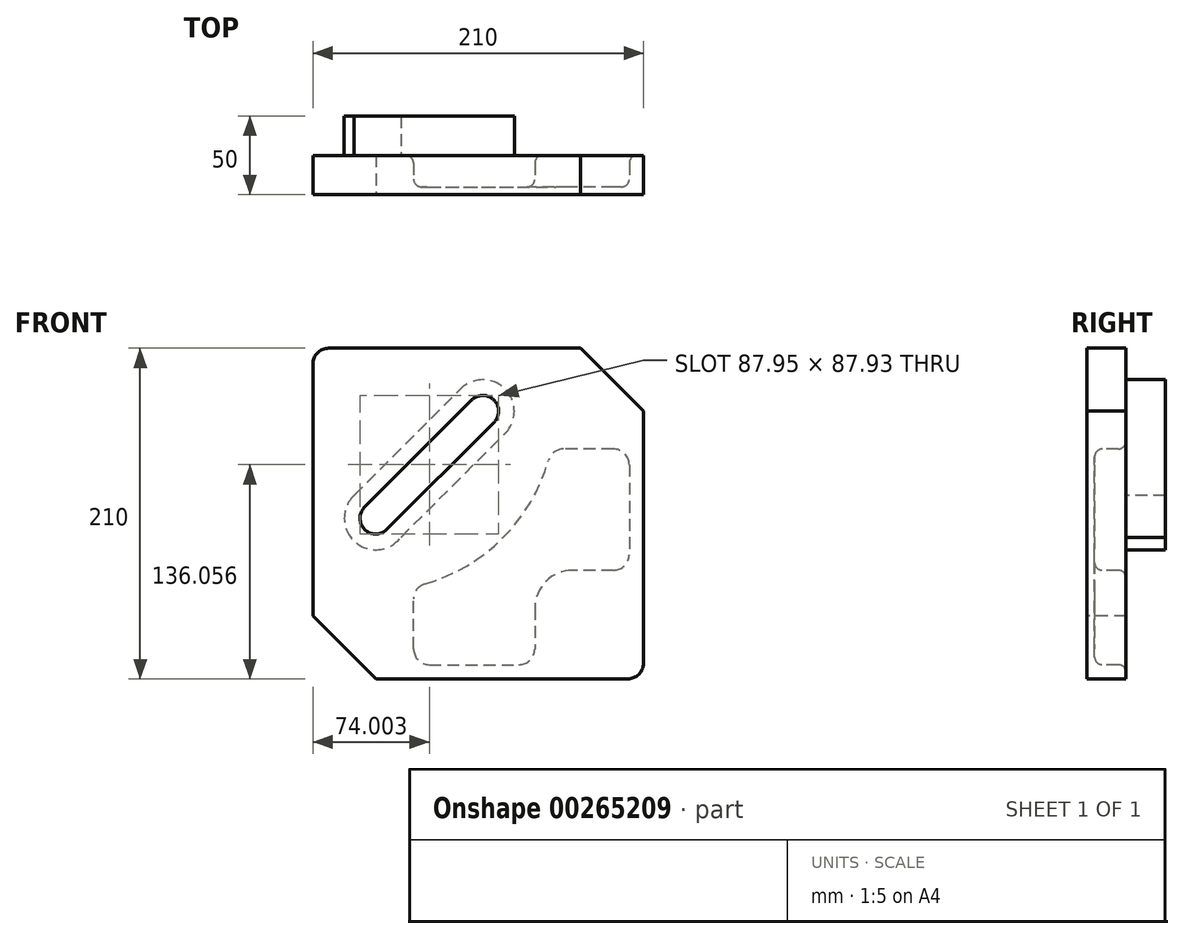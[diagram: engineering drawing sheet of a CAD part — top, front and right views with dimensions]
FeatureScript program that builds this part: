
annotation { "Feature Type Name" : "Feature", "Feature Type Description" : "" }
export const myFeature = defineFeature(function(context is Context, id is Id, definition is map)
    precondition{}
    {
        {
            var Q0;
            Q0=qCreatedBy(makeId("Front.planeOp"),FACE);
            var sketch = newSketch(context, id + "F0", { "sketchPlane" : qUnion([Q0])});
            skLineSegment(sketch, "E0", {"start": v(62.02, 39.98) * mm, "end": v(102.02, -0.02) * mm});
            skPoint(sketch, "E1.end.orphan", {"position": v(-107.98, -130.02) * mm});
            skLineSegment(sketch, "E2", {"start": v(62.02, 39.98) * mm, "end": v(-97.98, 39.98) * mm});
            skLineSegment(sketch, "E3", {"start": v(102.02, -0.02) * mm, "end": v(102.02, -160.02) * mm});
            skLineSegment(sketch, "E4", {"start": v(92.02, -170.02) * mm, "end": v(-67.98, -170.02) * mm});
            skLineSegment(sketch, "E5", {"start": v(-107.98, 29.98) * mm, "end": v(-107.98, -130.02) * mm});
            skLineSegment(sketch, "E6", {"start": v(-67.98, -170.02) * mm, "end": v(-107.98, -130.02) * mm});
            skArc(sketch, "E7", {"start": v(7.06, -7.08) * mm, "mid": v(7.07, 7.07) * mm, "end": v(-7.07, 7.07) * mm});
            skArc(sketch, "E8", {"start": v(-74.7, -60.61) * mm, "mid": v(-75.75, -74.31) * mm, "end": v(-62.14, -76.13) * mm});
            skArc(sketch, "E9", {"start": v(-81.65, -53.41) * mm, "mid": v(-81.42, -82.83) * mm, "end": v(-52.11, -80.19) * mm});
            skArc(sketch, "E10", {"start": v(14.12, -14.16) * mm, "mid": v(14.15, 14.13) * mm, "end": v(-14.15, 14.14) * mm});
            skLineSegment(sketch, "E11", {"start": v(-52.11, -80.19) * mm, "end": v(14.12, -14.16) * mm});
            skLineSegment(sketch, "E12", {"start": v(-81.65, -53.41) * mm, "end": v(-14.15, 14.14) * mm});
            skLineSegment(sketch, "E13", {"start": v(-74.7, -60.61) * mm, "end": v(-7.07, 7.07) * mm});
            skLineSegment(sketch, "E14", {"start": v(-62.14, -76.13) * mm, "end": v(7.06, -7.08) * mm});
            skPoint(sketch, "E15.orphan", {"position": v(14.16, 0) * mm});
            skPoint(sketch, "E16.orphan", {"position": v(0, 14.15) * mm});
            skPoint(sketch, "E17.visualSharp", {"position": v(-107.98, 39.98) * mm});
            skArc(sketch, "E17.filletArc", {"start": v(-97.98, 39.98) * mm, "mid": v(-105.06, 37.06) * mm, "end": v(-107.98, 29.98) * mm});
            skPoint(sketch, "E18.visualSharp", {"position": v(102.02, -170.02) * mm});
            skArc(sketch, "E18.filletArc", {"start": v(92.02, -170.02) * mm, "mid": v(99.09, -167.09) * mm, "end": v(102.02, -160.02) * mm});
            skLineSegment(sketch, "E19", {"start": v(83.02, -101.02) * mm, "end": v(57.02, -101.02) * mm});
            skLineSegment(sketch, "E20", {"start": v(33.02, -125.02) * mm, "end": v(33.02, -151.02) * mm});
            skPoint(sketch, "E21.visualSharp", {"position": v(33.02, -101.02) * mm});
            skArc(sketch, "E21.filletArc", {"start": v(57.02, -101.02) * mm, "mid": v(40.05, -108.05) * mm, "end": v(33.02, -125.02) * mm});
            skLineSegment(sketch, "E22", {"start": v(-43.98, -151.02) * mm, "end": v(-43.98, -119.26) * mm});
            skLineSegment(sketch, "E23", {"start": v(83.02, -24.02) * mm, "end": v(51.26, -24.02) * mm});
            skLineSegment(sketch, "E24", {"start": v(93.02, -34.02) * mm, "end": v(93.02, -91.02) * mm});
            skLineSegment(sketch, "E25", {"start": v(-33.98, -161.02) * mm, "end": v(23.02, -161.02) * mm});
            skPoint(sketch, "E26.newPointA", {"position": v(33.02, -170.02) * mm});
            skArc(sketch, "E26.filletArc", {"start": v(23.02, -161.02) * mm, "mid": v(30.09, -158.09) * mm, "end": v(33.02, -151.02) * mm});
            skPoint(sketch, "E27.newPointB", {"position": v(102.02, -101.02) * mm});
            skArc(sketch, "E27.filletArc", {"start": v(83.02, -101.02) * mm, "mid": v(90.09, -98.09) * mm, "end": v(93.02, -91.02) * mm});
            skPoint(sketch, "E28.newPointA", {"position": v(102.02, -24.02) * mm});
            skArc(sketch, "E28.filletArc", {"start": v(93.02, -34.02) * mm, "mid": v(90.09, -26.94) * mm, "end": v(83.02, -24.02) * mm});
            skPoint(sketch, "E29.newPointA", {"position": v(-43.98, -170.02) * mm});
            skArc(sketch, "E29.filletArc", {"start": v(-43.98, -151.02) * mm, "mid": v(-41.06, -158.09) * mm, "end": v(-33.98, -161.02) * mm});
            skPoint(sketch, "E30.orphan", {"position": v(33.02, -24.02) * mm});
            skArc(sketch, "E31.trimOffspring", {"start": v(-36.73, -109.65) * mm, "mid": v(12.63, -80.63) * mm, "end": v(41.65, -31.27) * mm});
            skPoint(sketch, "E32.visualSharp", {"position": v(43.46, -24.02) * mm});
            skArc(sketch, "E32.filletArc", {"start": v(51.26, -24.02) * mm, "mid": v(45.24, -26.03) * mm, "end": v(41.65, -31.27) * mm});
            skPoint(sketch, "E33.newPointB", {"position": v(-43.98, -101.02) * mm});
            skArc(sketch, "E33.filletArc", {"start": v(-36.73, -109.65) * mm, "mid": v(-41.97, -113.24) * mm, "end": v(-43.98, -119.26) * mm});
            skPoint(sketch, "E34.end.orphan", {"position": v(102.02, -33.02) * mm});
            skSolve(sketch);
        }
        {
            var Q0;
            Q0=makeQuery(id+"F0.imprint","IMPRINT",FACE,{"disambiguationData":[TD([[makeQuery(id+"F0.imprint","IMPRINT",EDGE,{"derivedFrom":sQuery(id+"F0.wireOp",EDGE,"E7")}),-1.0]])]});
            extrude(context, id + "F1", {"entities" : qUnion([Q0]), "oppositeDirection" : true, "depth" : 50 * mm});
        }
        {
            var Q0;
            Q0 = qSketchRegion(id + "F0", true);
            extrude(context, id + "F2", {"entities" : qUnion([Q0]), "operationType" : NewBodyOperationType.ADD, "oppositeDirection" : true, "depth" : 25 * mm});
        }
        {
            var Q0;
            {var subQ0=sQuery(id+"F0.wireOp",EDGE,"E12");var subQ1=sQuery(id+"F0.wireOp",EDGE,"E11");var subQ2=sQuery(id+"F0.wireOp",EDGE,"E10");var subQ3=sQuery(id+"F0.wireOp",EDGE,"E9");Q0=makeQuery(id+"F2.boolean.opBoolean","MERGE",FACE,{"derivedFrom":[makeQuery(id+"F1.opExtrude","CAP_FACE",FACE,{"disambiguationData":[OSD([sQuery(id+"F0.wireOp",EDGE,"E7"),sQuery(id+"F0.wireOp",EDGE,"E8"),subQ3,subQ2,subQ1,subQ0,sQuery(id+"F0.wireOp",EDGE,"E13"),sQuery(id+"F0.wireOp",EDGE,"E14")])],"isStart":true}),makeQuery(id+"F2.opExtrude","CAP_FACE",FACE,{"disambiguationData":[OSD([sQuery(id+"F0.wireOp",EDGE,"E0"),sQuery(id+"F0.wireOp",EDGE,"E2"),sQuery(id+"F0.wireOp",EDGE,"E3"),sQuery(id+"F0.wireOp",EDGE,"E4"),sQuery(id+"F0.wireOp",EDGE,"E5"),sQuery(id+"F0.wireOp",EDGE,"E6"),subQ3,subQ2,subQ1,subQ0,sQuery(id+"F0.wireOp",EDGE,"E17.filletArc"),sQuery(id+"F0.wireOp",EDGE,"E18.filletArc"),sQuery(id+"F0.wireOp",EDGE,"E19"),sQuery(id+"F0.wireOp",EDGE,"E20"),sQuery(id+"F0.wireOp",EDGE,"E21.filletArc"),sQuery(id+"F0.wireOp",EDGE,"E22"),sQuery(id+"F0.wireOp",EDGE,"E23"),sQuery(id+"F0.wireOp",EDGE,"E24"),sQuery(id+"F0.wireOp",EDGE,"E25"),sQuery(id+"F0.wireOp",EDGE,"E26.filletArc"),sQuery(id+"F0.wireOp",EDGE,"E27.filletArc"),sQuery(id+"F0.wireOp",EDGE,"E28.filletArc"),sQuery(id+"F0.wireOp",EDGE,"E29.filletArc"),sQuery(id+"F0.wireOp",EDGE,"E31.trimOffspring"),sQuery(id+"F0.wireOp",EDGE,"E32.filletArc"),sQuery(id+"F0.wireOp",EDGE,"E33.filletArc")])],"isStart":true})]});}
            var sketch = newSketch(context, id + "F3", { "sketchPlane" : qUnion([Q0])});
            skSolve(sketch);
        }
        {
            var Q0;
            Q0=makeQuery(id+"F3.imprint","IMPRINT",FACE,{"disambiguationData":[TD([[makeQuery(id+"F3.imprint","IMPRINT",EDGE,{"derivedFrom":makeQuery(id+"F2.opExtrude","CAP_EDGE",EDGE,{"disambiguationData":[OSD([sQuery(id+"F0.wireOp",EDGE,"E19")])],"isStart":true})}),-1.0]])]});
            extrude(context, id + "F4", {"entities" : qUnion([Q0]), "operationType" : NewBodyOperationType.ADD, "oppositeDirection" : true, "depth" : 5 * mm});
        }
        {
            var Q0;
            Q0=makeQuery(id+"F2.opExtrude","SWEPT_FACE",FACE,{"disambiguationData":[OSD([sQuery(id+"F0.wireOp",EDGE,"E23")])]});
            var Q1;
            Q1=makeQuery(id+"F4.opExtrude","CAP_FACE",FACE,{"disambiguationData":[OSD([sQuery(id+"F0.wireOp",EDGE,"E19"),sQuery(id+"F0.wireOp",EDGE,"E20"),sQuery(id+"F0.wireOp",EDGE,"E21.filletArc"),sQuery(id+"F0.wireOp",EDGE,"E22"),sQuery(id+"F0.wireOp",EDGE,"E23"),sQuery(id+"F0.wireOp",EDGE,"E24"),sQuery(id+"F0.wireOp",EDGE,"E25"),sQuery(id+"F0.wireOp",EDGE,"E26.filletArc"),sQuery(id+"F0.wireOp",EDGE,"E27.filletArc"),sQuery(id+"F0.wireOp",EDGE,"E28.filletArc"),sQuery(id+"F0.wireOp",EDGE,"E29.filletArc"),sQuery(id+"F0.wireOp",EDGE,"E31.trimOffspring"),sQuery(id+"F0.wireOp",EDGE,"E32.filletArc"),sQuery(id+"F0.wireOp",EDGE,"E33.filletArc")])],"isStart":false});
            fillet(context, id + "F5", {"entities" : qUnion([Q0, Q1]), "radius" : 5 * mm, "tangentPropagation" : true, "allowEdgeOverflow" : false});
        }
    });
